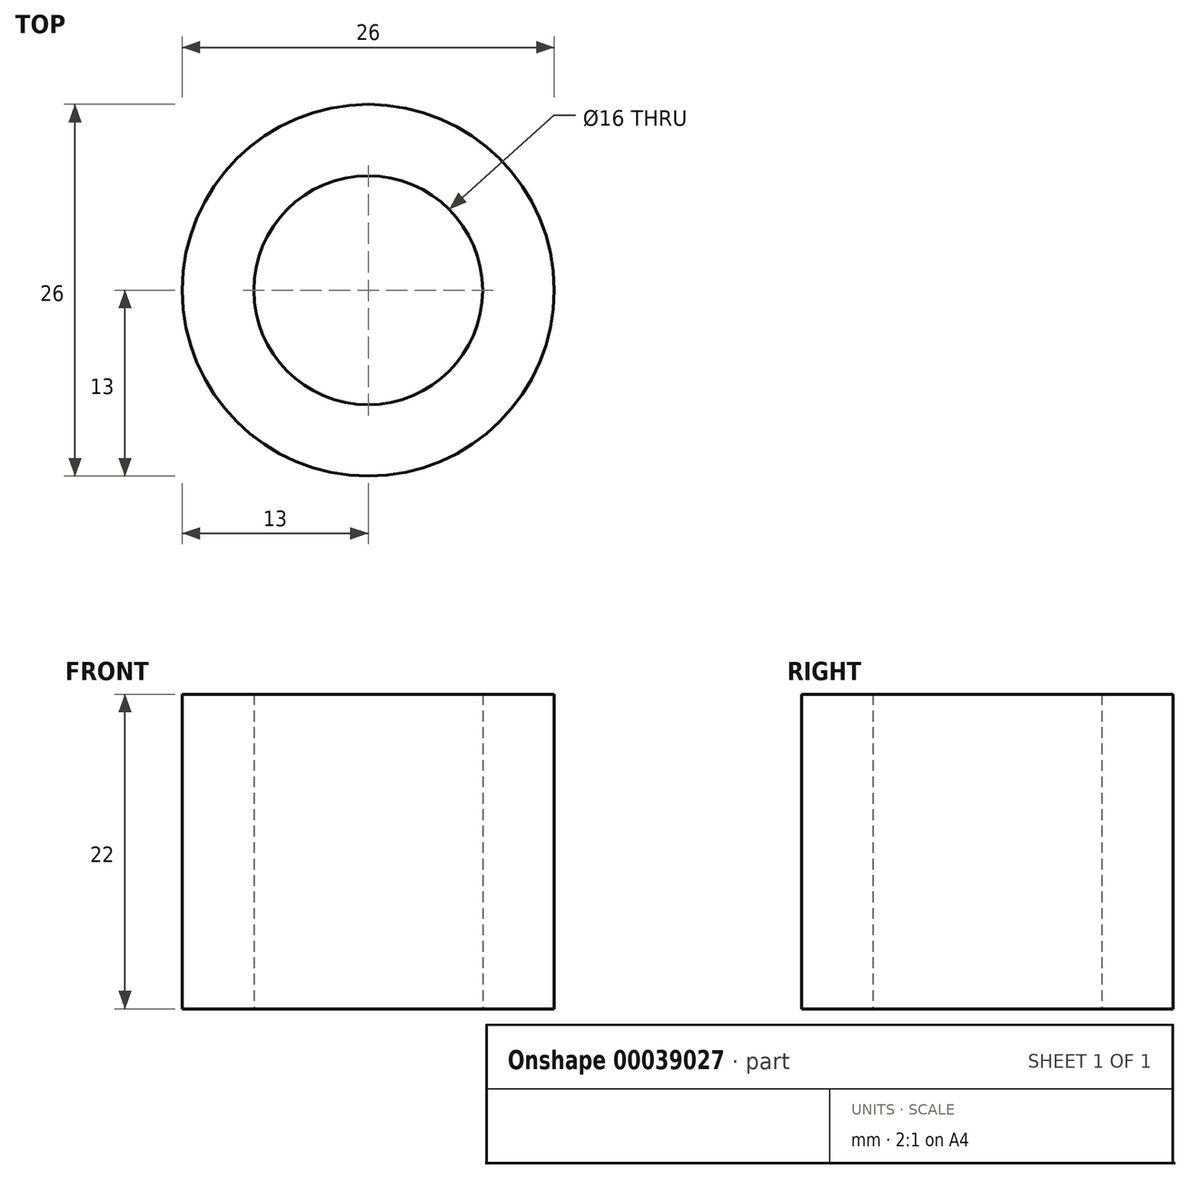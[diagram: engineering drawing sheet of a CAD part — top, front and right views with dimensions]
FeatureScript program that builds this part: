
annotation { "Feature Type Name" : "Feature", "Feature Type Description" : "" }
export const myFeature = defineFeature(function(context is Context, id is Id, definition is map)
    precondition{}
    {
        {
            var Q0;
            Q0=qCreatedBy(makeId("Top.planeOp"),FACE);
            var sketch = newSketch(context, id + "F0", { "sketchPlane" : qUnion([Q0])});
            skCircle(sketch, "E0", {"center": v(0, 0) * mm, "radius": 8 * mm});
            skCircle(sketch, "E1", {"center": v(0, 0) * mm, "radius": 13 * mm});
            skSolve(sketch);
        }
        {
            var Q0;
            Q0=makeQuery(id+"F0.imprint","IMPRINT",FACE,{"disambiguationData":[TD([[makeQuery(id+"F0.imprint","IMPRINT",EDGE,{"derivedFrom":sQuery(id+"F0.wireOp",EDGE,"E0")}),-1.0]])]});
            extrude(context, id + "F1", {"entities" : qUnion([Q0]), "depth" : 22 * mm});
        }
    });
